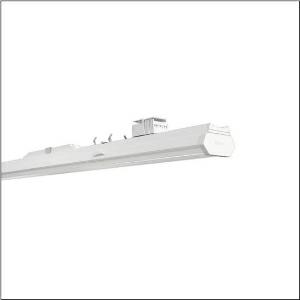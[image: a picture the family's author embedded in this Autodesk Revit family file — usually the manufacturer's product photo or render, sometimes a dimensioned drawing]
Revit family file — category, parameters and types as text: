
# Revit family: licross_r__11_protected_mo_51tp11dn49xf_977d
name_source: partatom
category: Lighting Fixtures
units: mm (PartAtom-declared; Revit-internal decimal feet)

## family parameters
Cut with Voids When Loaded = No
Host = Face
Light Source = No
Part Type = Normal
Room Calculation Point = No
Round Connector Dimension = Use Diameter
Shared = No

## types (1)
- --- (1 x LED, 9080 lm, 56.9 W, 4000K)
    Apparent Load = 57 VA
    CIE Flux Codes = 83 94 98 100 100
    Color Rendering = 80
    Color Temperature = 4000K
    Default Elevation = 1800 mm
    Description = Licross® 11 Protected MOluminaire insert, length: 1.500mm, width: 90mm, height: 101mm, LED rated luminous flux: 9.080lm, light colour: 840, control gear: DALI 2, control gear: ECG DALI, with plug, 5-pole, with phase selection, mains connection: 220..240V, AC, 50/60Hz, halogen-free wiring, primary optical cover: cover, of PMMA, light emission: direct with ceiling illumination distribution, protection rating (complete): IP64, insulation class (complete): insulation class I (protective earthing), certification: CE, ENEC, VDE, protection symbol: D if used in an environment with conductive dust loads with corresponding accessories, permissible ambient temperature for indoor applications: -25..+40°C, reducing of maximum allowable ambient temperature of 5°C with ceiling mounting, corresponds to IFS (International Featured Standards) requirements for safety and quality in the food industry, packaging unit: 1 piece
    Height = 92 mm
    Lamp = 1 x LED
    Lamp Light Flux = 9080 lm
    Lamp Power = 56.9 W
    Lamp count = 1
    Length = 1500 mm
    Luminous efficacy = 160 lm/W
    Manufacturer = Siteco
    ModVariant = No
    Model = 51TP11DN49XF
    Mounting Place = Ceiling
    Mounting Type = Pendant
    Number of Poles = 1
    OnlyDefault = Yes
    Power Factor = 1
    Product Name = Licross® 11 Protected MO
    Product group = luminaire insert
    ProductGroupID = 902
    Protection Class = Protection class I
    Protection Degree = IP 64
    RLX_Detail_Level = 1
    RlxData = <blob elided: 23693 chars, md5=b117fd13>
    Socket = socket
    Standby Power = 0 W
    System Light Flux = 9080 lm
    System Power = 57 W
    Type Comments = factory setting: luminous flux: 100 % | dim-lin: 254 | 375 mA
    Type Image = l_1256148.jpg
    URL = http://relux.com
    VarID = @adj_137621
    Voltage = 0 V
    Weight = 0.00 kg
    Width = 88 mm

## geometry (parser evidence)
native form markers: Blend x4, Sweep x13
no freeform markers — native parametric forms only
